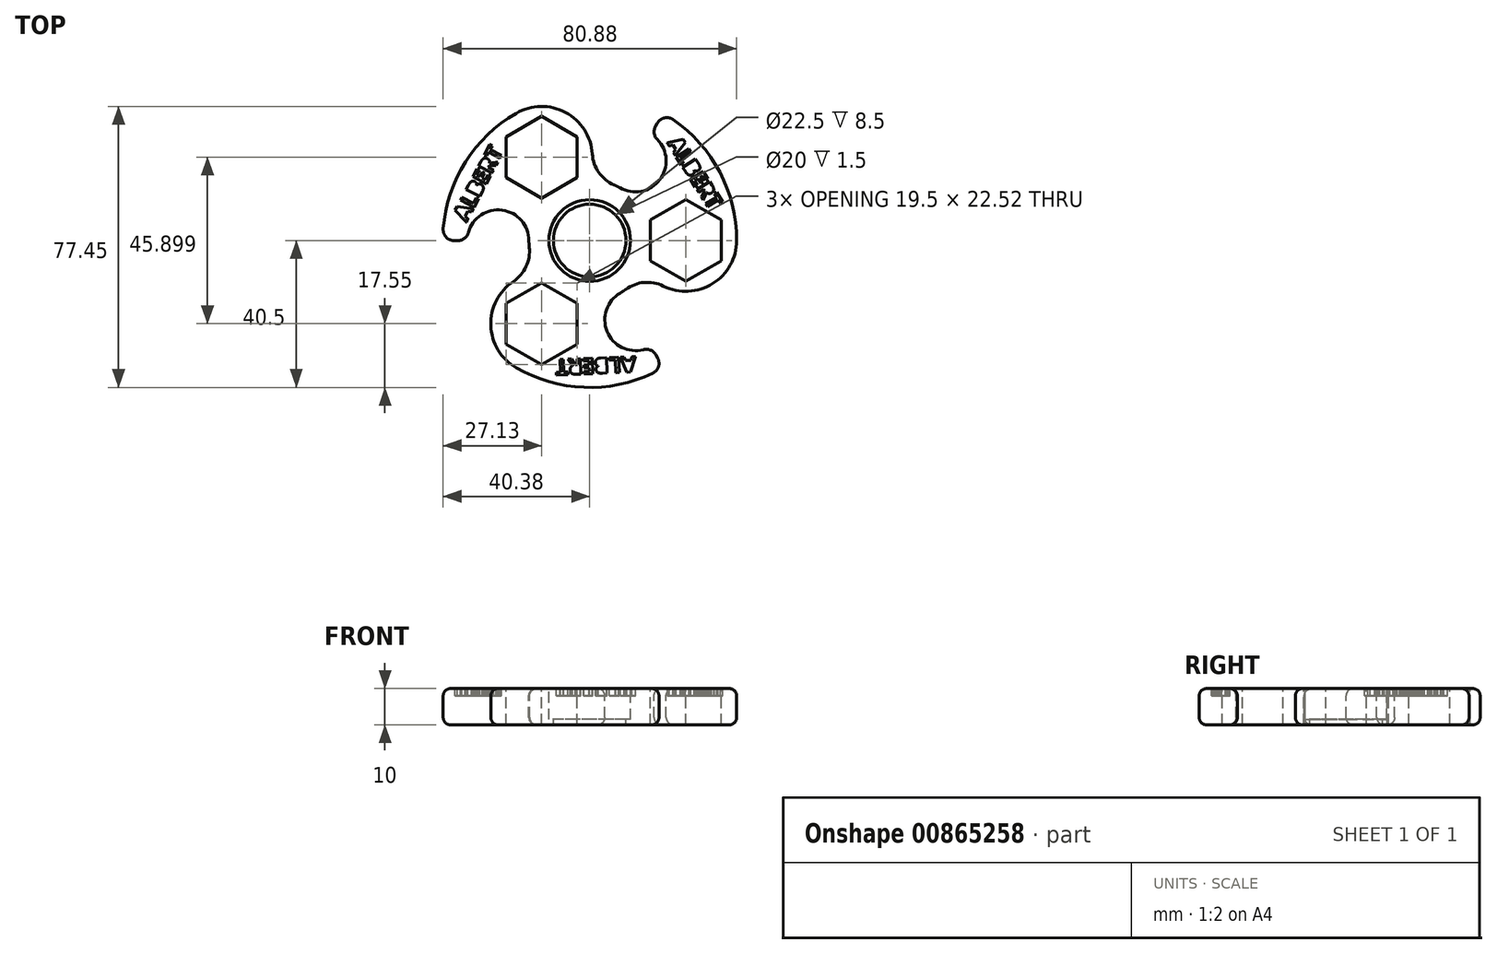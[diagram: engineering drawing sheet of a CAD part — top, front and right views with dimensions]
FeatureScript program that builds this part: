
annotation { "Feature Type Name" : "Feature", "Feature Type Description" : "" }
export const myFeature = defineFeature(function(context is Context, id is Id, definition is map)
    precondition{}
    {
        {
            var Q0;
            Q0=qCreatedBy(makeId("Top.planeOp"),FACE);
            var sketch = newSketch(context, id + "F0", { "sketchPlane" : qUnion([Q0])});
            skCircle(sketch, "E0", {"center": v(0, 0) * mm, "radius": 11.25 * mm});
            skCircle(sketch, "E1.cCircle", {"center": v(26.5, 0) * mm, "radius": 9.75 * mm, "construction": true});
            skLineSegment(sketch, "E1.0", {"start": v(36.25, 5.63) * mm, "end": v(36.25, -5.63) * mm});
            skLineSegment(sketch, "E1.1", {"start": v(36.25, -5.63) * mm, "end": v(26.5, -11.26) * mm});
            skLineSegment(sketch, "E1.2", {"start": v(26.5, -11.26) * mm, "end": v(16.75, -5.63) * mm});
            skLineSegment(sketch, "E1.3", {"start": v(16.75, -5.63) * mm, "end": v(16.75, 5.63) * mm});
            skLineSegment(sketch, "E1.4", {"start": v(16.75, 5.63) * mm, "end": v(26.5, 11.26) * mm});
            skLineSegment(sketch, "E1.5", {"start": v(26.5, 11.26) * mm, "end": v(36.25, 5.63) * mm});
            skPoint(sketch, "E1.0.midPoint", {"position": v(9.75, 0) * mm});
            skLineSegment(sketch, "E2", {"start": v(26.5, 11.26) * mm, "end": v(16.75, 5.63) * mm});
            skLineSegment(sketch, "E3", {"start": v(16.75, 5.63) * mm, "end": v(16.75, -5.63) * mm});
            skLineSegment(sketch, "E4", {"start": v(16.75, -5.63) * mm, "end": v(26.5, -11.26) * mm});
            skLineSegment(sketch, "E5", {"start": v(26.5, -11.26) * mm, "end": v(36.25, -5.63) * mm});
            skLineSegment(sketch, "E6", {"start": v(36.25, -5.63) * mm, "end": v(36.25, 5.63) * mm});
            skLineSegment(sketch, "E7", {"start": v(36.25, 5.63) * mm, "end": v(26.5, 11.26) * mm});
            skArc(sketch, "E8", {"start": v(8.38, 14.5) * mm, "mid": v(7.55, 14.95) * mm, "end": v(6.7, 15.35) * mm});
            skArc(sketch, "E9", {"start": v(20.3, -12.56) * mm, "mid": v(33.9, -11.89) * mm, "end": v(40.5, 0) * mm});
            skArc(sketch, "E10", {"start": v(40.5, 0) * mm, "mid": v(35.85, 18.84) * mm, "end": v(22.97, 33.35) * mm});
            skLineSegment(sketch, "E11", {"start": v(8.32, 14.54) * mm, "end": v(8.32, 14.54) * mm});
            skArc(sketch, "E12", {"start": v(8.32, 14.54) * mm, "mid": v(19.3, 16.7) * mm, "end": v(18.62, 27.87) * mm});
            skLineSegment(sketch, "E13.trimOffspring", {"start": v(18.16, 31.5) * mm, "end": v(18.68, 32.39) * mm});
            skPoint(sketch, "E14.visualSharp", {"position": v(14.85, -7.76) * mm});
            skArc(sketch, "E14.filletArc", {"start": v(20.3, -12.56) * mm, "mid": v(15, -11.56) * mm, "end": v(9.95, -13.48) * mm});
            skPoint(sketch, "E15.visualSharp", {"position": v(20.24, 35.08) * mm});
            skArc(sketch, "E15.filletArc", {"start": v(22.97, 33.35) * mm, "mid": v(20.62, 33.8) * mm, "end": v(18.68, 32.39) * mm});
            skPoint(sketch, "E16.visualSharp", {"position": v(16.85, 29.24) * mm});
            skArc(sketch, "E16.filletArc", {"start": v(18.16, 31.5) * mm, "mid": v(17.78, 29.6) * mm, "end": v(18.62, 27.87) * mm});
            skArc(sketch, "E17.1.0", {"start": v(-16.75, -0.07) * mm, "mid": v(-24.11, 8.38) * mm, "end": v(-33.45, 2.19) * mm});
            skArc(sketch, "E17.1.1", {"start": v(-36.35, -0.02) * mm, "mid": v(-34.53, 0.6) * mm, "end": v(-33.45, 2.19) * mm});
            skLineSegment(sketch, "E17.1.2", {"start": v(-36.35, -0.02) * mm, "end": v(-37.39, -0.02) * mm});
            skArc(sketch, "E17.1.3", {"start": v(-40.37, 3.22) * mm, "mid": v(-39.59, 0.95) * mm, "end": v(-37.39, -0.02) * mm});
            skArc(sketch, "E17.1.4", {"start": v(-20.25, 35.07) * mm, "mid": v(-34.24, 21.63) * mm, "end": v(-40.37, 3.22) * mm});
            skArc(sketch, "E17.1.5", {"start": v(0.72, 23.86) * mm, "mid": v(-6.65, 35.3) * mm, "end": v(-20.25, 35.07) * mm});
            skArc(sketch, "E17.1.6", {"start": v(0.72, 23.86) * mm, "mid": v(2.52, 18.77) * mm, "end": v(6.7, 15.35) * mm});
            skLineSegment(sketch, "E17.1.7", {"start": v(-3.5, 17.32) * mm, "end": v(-3.5, 28.58) * mm});
            skLineSegment(sketch, "E17.1.8", {"start": v(-3.5, 28.58) * mm, "end": v(-13.25, 34.2) * mm});
            skLineSegment(sketch, "E17.1.9", {"start": v(-13.25, 34.2) * mm, "end": v(-23, 28.58) * mm});
            skLineSegment(sketch, "E17.1.10", {"start": v(-23, 28.58) * mm, "end": v(-23, 17.32) * mm});
            skLineSegment(sketch, "E17.1.11", {"start": v(-23, 17.32) * mm, "end": v(-13.25, 11.7) * mm});
            skLineSegment(sketch, "E17.1.12", {"start": v(-13.25, 11.7) * mm, "end": v(-3.5, 17.32) * mm});
            skArc(sketch, "E17.2.0", {"start": v(8.43, -14.47) * mm, "mid": v(4.8, -25.07) * mm, "end": v(14.83, -30.06) * mm});
            skArc(sketch, "E17.2.1", {"start": v(18.2, -31.47) * mm, "mid": v(16.75, -30.2) * mm, "end": v(14.83, -30.06) * mm});
            skLineSegment(sketch, "E17.2.2", {"start": v(18.2, -31.47) * mm, "end": v(18.71, -32.37) * mm});
            skArc(sketch, "E17.2.3", {"start": v(17.4, -36.57) * mm, "mid": v(18.97, -34.76) * mm, "end": v(18.71, -32.37) * mm});
            skArc(sketch, "E17.2.4", {"start": v(-20.25, -35.07) * mm, "mid": v(-1.61, -40.47) * mm, "end": v(17.4, -36.57) * mm});
            skArc(sketch, "E17.2.5", {"start": v(-21.03, -11.3) * mm, "mid": v(-27.24, -23.4) * mm, "end": v(-20.25, -35.07) * mm});
            skArc(sketch, "E17.2.6", {"start": v(-21.03, -11.3) * mm, "mid": v(-17.51, -7.2) * mm, "end": v(-16.64, -1.87) * mm});
            skLineSegment(sketch, "E17.2.7", {"start": v(-13.25, -11.7) * mm, "end": v(-23, -17.32) * mm});
            skLineSegment(sketch, "E17.2.8", {"start": v(-23, -17.32) * mm, "end": v(-23, -28.58) * mm});
            skLineSegment(sketch, "E17.2.9", {"start": v(-23, -28.58) * mm, "end": v(-13.25, -34.2) * mm});
            skLineSegment(sketch, "E17.2.10", {"start": v(-13.25, -34.2) * mm, "end": v(-3.5, -28.58) * mm});
            skLineSegment(sketch, "E17.2.11", {"start": v(-3.5, -28.58) * mm, "end": v(-3.5, -17.32) * mm});
            skLineSegment(sketch, "E17.2.12", {"start": v(-3.5, -17.32) * mm, "end": v(-13.25, -11.7) * mm});
            skArc(sketch, "E18.trimOffspring", {"start": v(-16.75, 0) * mm, "mid": v(-16.72, -0.94) * mm, "end": v(-16.64, -1.87) * mm});
            skArc(sketch, "E19.trimOffspring", {"start": v(8.37, -14.5) * mm, "mid": v(9.17, -14.02) * mm, "end": v(9.95, -13.48) * mm});
            skSolve(sketch);
        }
        {
            var Q0;
            Q0=qCreatedBy(makeId("Top.planeOp"),FACE);
            cPlane(context, id + "F1", {"entities" : qUnion([Q0]), "cplaneType" : CPlaneType.OFFSET, "offset" : 5 * mm, "width" : 150 * mm, "height" : 150 * mm});
        }
        {
            var Q0;
            Q0=qCreatedBy(id+"F1.planeOp",FACE);
            var sketch = newSketch(context, id + "F2", { "sketchPlane" : qUnion([Q0])});
            skText(sketch, "E20", { "text": "ALBERT", "fontName": "OpenSans-Bold.ttf"});
            const initialGuessF2  = {"E20": [0.0214, 0.0269, 0.53415, -0.84539, 0.00426]};
            skSetInitialGuess(sketch, initialGuessF2);
            skSolve(sketch);
        }
        {
            var Q0;
            Q0=qCreatedBy(makeId("Top.planeOp"),FACE);
            var sketch = newSketch(context, id + "F3", { "sketchPlane" : qUnion([Q0])});
            skCircle(sketch, "E21", {"center": v(0, 0) * mm, "radius": 11.25 * mm});
            skCircle(sketch, "E22", {"center": v(0, 0) * mm, "radius": 10 * mm});
            skSolve(sketch);
        }
        {
            var Q0;
            Q0=makeQuery(id+"F0.imprint","IMPRINT",FACE,{"disambiguationData":[TD([[makeQuery(id+"F0.imprint","IMPRINT",EDGE,{"derivedFrom":sQuery(id+"F0.wireOp",EDGE,"E0")}),-1.0]])]});
            extrude(context, id + "F4", {"entities" : qUnion([Q0]), "depth" : -10 * mm, "offsetDistance" : 25 * mm});
        }
        {
            var Q0;
            Q0=makeQuery(id+"F3.imprint","IMPRINT",FACE,{"disambiguationData":[TD([[makeQuery(id+"F3.imprint","IMPRINT",EDGE,{"derivedFrom":sQuery(id+"F3.wireOp",EDGE,"E21")}),1.0]])]});
            extrude(context, id + "F5", {"entities" : qUnion([Q0]), "oppositeDirection" : true, "depth" : 1 * mm, "offsetDistance" : 25 * mm});
        }
        {
            var Q0;
            Q0=qSketchRegion(id+"F2",true);
            extrude(context, id + "F6", {"entities" : qUnion([Q0]), "depth" : -7 * mm, "offsetDistance" : 25 * mm});
        }
        {
            var Q0;
            Q0=makeQuery(id+"F4.opExtrude","CAP_EDGE",EDGE,{"disambiguationData":[OSD([sQuery(id+"F0.wireOp",EDGE,"E17.1.4")])],"isStart":true});
            var Q1;
            Q1=makeQuery(id+"F4.opExtrude","CAP_EDGE",EDGE,{"disambiguationData":[OSD([sQuery(id+"F0.wireOp",EDGE,"E17.1.5")])],"isStart":true});
            var Q2;
            Q2=makeQuery(id+"F4.opExtrude","CAP_EDGE",EDGE,{"disambiguationData":[OSD([sQuery(id+"F0.wireOp",EDGE,"E12")])],"isStart":true});
            var Q3;
            Q3=makeQuery(id+"F4.opExtrude","CAP_EDGE",EDGE,{"disambiguationData":[OSD([sQuery(id+"F0.wireOp",EDGE,"E17.2.2")])],"isStart":true});
            fillet(context, id + "F7", {"entities" : qUnion([Q0, Q1, Q2, Q3]), "radius" : 2 * mm, "tangentPropagation" : true, "allowEdgeOverflow" : false});
        }
        {
            var Q0;
            Q0=makeQuery(id+"F4.opExtrude","CAP_EDGE",EDGE,{"disambiguationData":[OSD([sQuery(id+"F0.wireOp",EDGE,"E17.2.4")])],"isStart":false});
            var Q1;
            Q1=makeQuery(id+"F4.opExtrude","CAP_EDGE",EDGE,{"disambiguationData":[OSD([sQuery(id+"F0.wireOp",EDGE,"E17.2.3")])],"isStart":false});
            var Q2;
            Q2=makeQuery(id+"F4.opExtrude","CAP_EDGE",EDGE,{"disambiguationData":[OSD([sQuery(id+"F0.wireOp",EDGE,"E9")])],"isStart":false});
            var Q3;
            Q3=makeQuery(id+"F4.opExtrude","CAP_EDGE",EDGE,{"disambiguationData":[OSD([sQuery(id+"F0.wireOp",EDGE,"E17.1.5")])],"isStart":false});
            fillet(context, id + "F8", {"entities" : qUnion([Q0, Q1, Q2, Q3]), "radius" : 2 * mm, "tangentPropagation" : true, "allowEdgeOverflow" : false});
        }
        {
            var Q0;
            Q0=makeQuery(id+"F6.opExtrude","SWEPT_BODY",BODY,{"disambiguationData":[OSD([sQuery(id+"F2.wireOp",EDGE,"E20.sketch_text.stroke-74"),sQuery(id+"F2.wireOp",EDGE,"E20.sketch_text.stroke-75"),sQuery(id+"F2.wireOp",EDGE,"E20.sketch_text.stroke-76"),sQuery(id+"F2.wireOp",EDGE,"E20.sketch_text.stroke-77"),sQuery(id+"F2.wireOp",EDGE,"E20.sketch_text.stroke-78"),sQuery(id+"F2.wireOp",EDGE,"E20.sketch_text.stroke-79"),sQuery(id+"F2.wireOp",EDGE,"E20.sketch_text.stroke-80"),sQuery(id+"F2.wireOp",EDGE,"E20.sketch_text.stroke-81")])]});
            var Q1;
            Q1=makeQuery(id+"F6.opExtrude","SWEPT_BODY",BODY,{"disambiguationData":[OSD([sQuery(id+"F2.wireOp",EDGE,"E20.sketch_text.stroke-55"),sQuery(id+"F2.wireOp",EDGE,"E20.sketch_text.stroke-56"),sQuery(id+"F2.wireOp",EDGE,"E20.sketch_text.stroke-57"),sQuery(id+"F2.wireOp",EDGE,"E20.sketch_text.stroke-58"),sQuery(id+"F2.wireOp",EDGE,"E20.sketch_text.stroke-59"),sQuery(id+"F2.wireOp",EDGE,"E20.sketch_text.stroke-60"),sQuery(id+"F2.wireOp",EDGE,"E20.sketch_text.stroke-61"),sQuery(id+"F2.wireOp",EDGE,"E20.sketch_text.stroke-62"),sQuery(id+"F2.wireOp",EDGE,"E20.sketch_text.stroke-63"),sQuery(id+"F2.wireOp",EDGE,"E20.sketch_text.stroke-64"),sQuery(id+"F2.wireOp",EDGE,"E20.sketch_text.stroke-65"),sQuery(id+"F2.wireOp",EDGE,"E20.sketch_text.stroke-66"),sQuery(id+"F2.wireOp",EDGE,"E20.sketch_text.stroke-67"),sQuery(id+"F2.wireOp",EDGE,"E20.sketch_text.stroke-68"),sQuery(id+"F2.wireOp",EDGE,"E20.sketch_text.stroke-69"),sQuery(id+"F2.wireOp",EDGE,"E20.sketch_text.stroke-70"),sQuery(id+"F2.wireOp",EDGE,"E20.sketch_text.stroke-71"),sQuery(id+"F2.wireOp",EDGE,"E20.sketch_text.stroke-72"),sQuery(id+"F2.wireOp",EDGE,"E20.sketch_text.stroke-73")])]});
            var Q2;
            Q2=makeQuery(id+"F6.opExtrude","SWEPT_BODY",BODY,{"disambiguationData":[OSD([sQuery(id+"F2.wireOp",EDGE,"E20.sketch_text.stroke-43"),sQuery(id+"F2.wireOp",EDGE,"E20.sketch_text.stroke-44"),sQuery(id+"F2.wireOp",EDGE,"E20.sketch_text.stroke-45"),sQuery(id+"F2.wireOp",EDGE,"E20.sketch_text.stroke-46"),sQuery(id+"F2.wireOp",EDGE,"E20.sketch_text.stroke-47"),sQuery(id+"F2.wireOp",EDGE,"E20.sketch_text.stroke-48"),sQuery(id+"F2.wireOp",EDGE,"E20.sketch_text.stroke-49"),sQuery(id+"F2.wireOp",EDGE,"E20.sketch_text.stroke-50"),sQuery(id+"F2.wireOp",EDGE,"E20.sketch_text.stroke-51"),sQuery(id+"F2.wireOp",EDGE,"E20.sketch_text.stroke-52"),sQuery(id+"F2.wireOp",EDGE,"E20.sketch_text.stroke-53"),sQuery(id+"F2.wireOp",EDGE,"E20.sketch_text.stroke-54")])]});
            var Q3;
            Q3=makeQuery(id+"F6.opExtrude","SWEPT_BODY",BODY,{"disambiguationData":[OSD([sQuery(id+"F2.wireOp",EDGE,"E20.sketch_text.stroke-18"),sQuery(id+"F2.wireOp",EDGE,"E20.sketch_text.stroke-19"),sQuery(id+"F2.wireOp",EDGE,"E20.sketch_text.stroke-20"),sQuery(id+"F2.wireOp",EDGE,"E20.sketch_text.stroke-21"),sQuery(id+"F2.wireOp",EDGE,"E20.sketch_text.stroke-22"),sQuery(id+"F2.wireOp",EDGE,"E20.sketch_text.stroke-23"),sQuery(id+"F2.wireOp",EDGE,"E20.sketch_text.stroke-24"),sQuery(id+"F2.wireOp",EDGE,"E20.sketch_text.stroke-25"),sQuery(id+"F2.wireOp",EDGE,"E20.sketch_text.stroke-26"),sQuery(id+"F2.wireOp",EDGE,"E20.sketch_text.stroke-27"),sQuery(id+"F2.wireOp",EDGE,"E20.sketch_text.stroke-28"),sQuery(id+"F2.wireOp",EDGE,"E20.sketch_text.stroke-29"),sQuery(id+"F2.wireOp",EDGE,"E20.sketch_text.stroke-30"),sQuery(id+"F2.wireOp",EDGE,"E20.sketch_text.stroke-31"),sQuery(id+"F2.wireOp",EDGE,"E20.sketch_text.stroke-32"),sQuery(id+"F2.wireOp",EDGE,"E20.sketch_text.stroke-33"),sQuery(id+"F2.wireOp",EDGE,"E20.sketch_text.stroke-34"),sQuery(id+"F2.wireOp",EDGE,"E20.sketch_text.stroke-35"),sQuery(id+"F2.wireOp",EDGE,"E20.sketch_text.stroke-36"),sQuery(id+"F2.wireOp",EDGE,"E20.sketch_text.stroke-37"),sQuery(id+"F2.wireOp",EDGE,"E20.sketch_text.stroke-38"),sQuery(id+"F2.wireOp",EDGE,"E20.sketch_text.stroke-39"),sQuery(id+"F2.wireOp",EDGE,"E20.sketch_text.stroke-40"),sQuery(id+"F2.wireOp",EDGE,"E20.sketch_text.stroke-41"),sQuery(id+"F2.wireOp",EDGE,"E20.sketch_text.stroke-42")])]});
            var Q4;
            Q4=makeQuery(id+"F6.opExtrude","SWEPT_BODY",BODY,{"disambiguationData":[OSD([sQuery(id+"F2.wireOp",EDGE,"E20.sketch_text.stroke-0"),sQuery(id+"F2.wireOp",EDGE,"E20.sketch_text.stroke-1"),sQuery(id+"F2.wireOp",EDGE,"E20.sketch_text.stroke-2"),sQuery(id+"F2.wireOp",EDGE,"E20.sketch_text.stroke-3"),sQuery(id+"F2.wireOp",EDGE,"E20.sketch_text.stroke-4"),sQuery(id+"F2.wireOp",EDGE,"E20.sketch_text.stroke-5"),sQuery(id+"F2.wireOp",EDGE,"E20.sketch_text.stroke-6"),sQuery(id+"F2.wireOp",EDGE,"E20.sketch_text.stroke-7"),sQuery(id+"F2.wireOp",EDGE,"E20.sketch_text.stroke-8"),sQuery(id+"F2.wireOp",EDGE,"E20.sketch_text.stroke-9"),sQuery(id+"F2.wireOp",EDGE,"E20.sketch_text.stroke-10"),sQuery(id+"F2.wireOp",EDGE,"E20.sketch_text.stroke-11")])]});
            var Q5;
            Q5=makeQuery(id+"F6.opExtrude","SWEPT_BODY",BODY,{"disambiguationData":[OSD([sQuery(id+"F2.wireOp",EDGE,"E20.sketch_text.stroke-12"),sQuery(id+"F2.wireOp",EDGE,"E20.sketch_text.stroke-13"),sQuery(id+"F2.wireOp",EDGE,"E20.sketch_text.stroke-14"),sQuery(id+"F2.wireOp",EDGE,"E20.sketch_text.stroke-15"),sQuery(id+"F2.wireOp",EDGE,"E20.sketch_text.stroke-16"),sQuery(id+"F2.wireOp",EDGE,"E20.sketch_text.stroke-17")])]});
            var Q6;
            Q6=makeQuery(id+"F5.opExtrude","CAP_EDGE",EDGE,{"disambiguationData":[OSD([sQuery(id+"F3.wireOp",EDGE,"E22")])],"isStart":false});
            circularPattern(context, id + "F9", {"operationType" : NewBodyOperationType.REMOVE, "entities" : qUnion([Q0, Q1, Q2, Q3, Q4, Q5]), "axis" : qUnion([Q6]), "angle" : 360 * degree, "instanceCount" : 3, "equalSpace" : true, "computeTransformsWithoutBuiltin" : true});
        }
        {
            var Q0;
            Q0=makeQuery(id+"F5.opExtrude","SWEPT_BODY",BODY,{"disambiguationData":[OSD([sQuery(id+"F3.wireOp",EDGE,"E21"),sQuery(id+"F3.wireOp",EDGE,"E22")])]});
            transform(context, id + "F10", {"entities" : qUnion([Q0]), "transformType" : TransformType.TRANSLATION_3D, "dx" : 0 * mm, "dy" : 0 * mm, "dz" : -9 * mm, "makeCopy" : false});
        }
        {
            var Q0;
            Q0=makeQuery(id+"F9.boolean.opBoolean","SPLIT",FACE,{"disambiguationData":[TD([makeQuery(id+"F9.opPattern","COPY",FACE,{"derivedFrom":makeQuery(id+"F6.opExtrude","SWEPT_FACE",FACE,{"disambiguationData":[OSD([sQuery(id+"F2.wireOp",EDGE,"E20.sketch_text.stroke-8")])]}),"instanceName":"1"})])],"derivedFrom":makeQuery(id+"F4.opExtrude","CAP_FACE",FACE,{"disambiguationData":[OSD([sQuery(id+"F0.wireOp",EDGE,"E0"),sQuery(id+"F0.wireOp",EDGE,"E2"),sQuery(id+"F0.wireOp",EDGE,"E3"),sQuery(id+"F0.wireOp",EDGE,"E4"),sQuery(id+"F0.wireOp",EDGE,"E5"),sQuery(id+"F0.wireOp",EDGE,"E6"),sQuery(id+"F0.wireOp",EDGE,"E7"),sQuery(id+"F0.wireOp",EDGE,"E8"),sQuery(id+"F0.wireOp",EDGE,"E9"),sQuery(id+"F0.wireOp",EDGE,"E10"),sQuery(id+"F0.wireOp",EDGE,"E12"),sQuery(id+"F0.wireOp",EDGE,"E13.trimOffspring"),sQuery(id+"F0.wireOp",EDGE,"E14.filletArc"),sQuery(id+"F0.wireOp",EDGE,"E15.filletArc"),sQuery(id+"F0.wireOp",EDGE,"E16.filletArc"),sQuery(id+"F0.wireOp",EDGE,"E17.1.0"),sQuery(id+"F0.wireOp",EDGE,"E17.1.1"),sQuery(id+"F0.wireOp",EDGE,"E17.1.2"),sQuery(id+"F0.wireOp",EDGE,"E17.1.3"),sQuery(id+"F0.wireOp",EDGE,"E17.1.4"),sQuery(id+"F0.wireOp",EDGE,"E17.1.5"),sQuery(id+"F0.wireOp",EDGE,"E17.1.6"),sQuery(id+"F0.wireOp",EDGE,"E17.1.7"),sQuery(id+"F0.wireOp",EDGE,"E17.1.8"),sQuery(id+"F0.wireOp",EDGE,"E17.1.9"),sQuery(id+"F0.wireOp",EDGE,"E17.1.10"),sQuery(id+"F0.wireOp",EDGE,"E17.1.11"),sQuery(id+"F0.wireOp",EDGE,"E17.1.12"),sQuery(id+"F0.wireOp",EDGE,"E17.2.0"),sQuery(id+"F0.wireOp",EDGE,"E17.2.1"),sQuery(id+"F0.wireOp",EDGE,"E17.2.2"),sQuery(id+"F0.wireOp",EDGE,"E17.2.3"),sQuery(id+"F0.wireOp",EDGE,"E17.2.4"),sQuery(id+"F0.wireOp",EDGE,"E17.2.5"),sQuery(id+"F0.wireOp",EDGE,"E17.2.6"),sQuery(id+"F0.wireOp",EDGE,"E17.2.7"),sQuery(id+"F0.wireOp",EDGE,"E17.2.8"),sQuery(id+"F0.wireOp",EDGE,"E17.2.9"),sQuery(id+"F0.wireOp",EDGE,"E17.2.10"),sQuery(id+"F0.wireOp",EDGE,"E17.2.11"),sQuery(id+"F0.wireOp",EDGE,"E17.2.12"),sQuery(id+"F0.wireOp",EDGE,"E18.trimOffspring"),sQuery(id+"F0.wireOp",EDGE,"E19.trimOffspring")])],"isStart":true})});
            var Q1;
            Q1=makeQuery(id+"F9.boolean.opBoolean","SPLIT",FACE,{"disambiguationData":[TD([makeQuery(id+"F9.opPattern","COPY",FACE,{"derivedFrom":makeQuery(id+"F6.opExtrude","SWEPT_FACE",FACE,{"disambiguationData":[OSD([sQuery(id+"F2.wireOp",EDGE,"E20.sketch_text.stroke-30")])]}),"instanceName":"1"})])],"derivedFrom":makeQuery(id+"F4.opExtrude","CAP_FACE",FACE,{"disambiguationData":[OSD([sQuery(id+"F0.wireOp",EDGE,"E0"),sQuery(id+"F0.wireOp",EDGE,"E2"),sQuery(id+"F0.wireOp",EDGE,"E3"),sQuery(id+"F0.wireOp",EDGE,"E4"),sQuery(id+"F0.wireOp",EDGE,"E5"),sQuery(id+"F0.wireOp",EDGE,"E6"),sQuery(id+"F0.wireOp",EDGE,"E7"),sQuery(id+"F0.wireOp",EDGE,"E8"),sQuery(id+"F0.wireOp",EDGE,"E9"),sQuery(id+"F0.wireOp",EDGE,"E10"),sQuery(id+"F0.wireOp",EDGE,"E12"),sQuery(id+"F0.wireOp",EDGE,"E13.trimOffspring"),sQuery(id+"F0.wireOp",EDGE,"E14.filletArc"),sQuery(id+"F0.wireOp",EDGE,"E15.filletArc"),sQuery(id+"F0.wireOp",EDGE,"E16.filletArc"),sQuery(id+"F0.wireOp",EDGE,"E17.1.0"),sQuery(id+"F0.wireOp",EDGE,"E17.1.1"),sQuery(id+"F0.wireOp",EDGE,"E17.1.2"),sQuery(id+"F0.wireOp",EDGE,"E17.1.3"),sQuery(id+"F0.wireOp",EDGE,"E17.1.4"),sQuery(id+"F0.wireOp",EDGE,"E17.1.5"),sQuery(id+"F0.wireOp",EDGE,"E17.1.6"),sQuery(id+"F0.wireOp",EDGE,"E17.1.7"),sQuery(id+"F0.wireOp",EDGE,"E17.1.8"),sQuery(id+"F0.wireOp",EDGE,"E17.1.9"),sQuery(id+"F0.wireOp",EDGE,"E17.1.10"),sQuery(id+"F0.wireOp",EDGE,"E17.1.11"),sQuery(id+"F0.wireOp",EDGE,"E17.1.12"),sQuery(id+"F0.wireOp",EDGE,"E17.2.0"),sQuery(id+"F0.wireOp",EDGE,"E17.2.1"),sQuery(id+"F0.wireOp",EDGE,"E17.2.2"),sQuery(id+"F0.wireOp",EDGE,"E17.2.3"),sQuery(id+"F0.wireOp",EDGE,"E17.2.4"),sQuery(id+"F0.wireOp",EDGE,"E17.2.5"),sQuery(id+"F0.wireOp",EDGE,"E17.2.6"),sQuery(id+"F0.wireOp",EDGE,"E17.2.7"),sQuery(id+"F0.wireOp",EDGE,"E17.2.8"),sQuery(id+"F0.wireOp",EDGE,"E17.2.9"),sQuery(id+"F0.wireOp",EDGE,"E17.2.10"),sQuery(id+"F0.wireOp",EDGE,"E17.2.11"),sQuery(id+"F0.wireOp",EDGE,"E17.2.12"),sQuery(id+"F0.wireOp",EDGE,"E18.trimOffspring"),sQuery(id+"F0.wireOp",EDGE,"E19.trimOffspring")])],"isStart":true})});
            var Q2;
            Q2=makeQuery(id+"F9.boolean.opBoolean","SPLIT",FACE,{"disambiguationData":[TD([makeQuery(id+"F9.opPattern","COPY",FACE,{"derivedFrom":makeQuery(id+"F6.opExtrude","SWEPT_FACE",FACE,{"disambiguationData":[OSD([sQuery(id+"F2.wireOp",EDGE,"E20.sketch_text.stroke-37")])]}),"instanceName":"1"})])],"derivedFrom":makeQuery(id+"F4.opExtrude","CAP_FACE",FACE,{"disambiguationData":[OSD([sQuery(id+"F0.wireOp",EDGE,"E0"),sQuery(id+"F0.wireOp",EDGE,"E2"),sQuery(id+"F0.wireOp",EDGE,"E3"),sQuery(id+"F0.wireOp",EDGE,"E4"),sQuery(id+"F0.wireOp",EDGE,"E5"),sQuery(id+"F0.wireOp",EDGE,"E6"),sQuery(id+"F0.wireOp",EDGE,"E7"),sQuery(id+"F0.wireOp",EDGE,"E8"),sQuery(id+"F0.wireOp",EDGE,"E9"),sQuery(id+"F0.wireOp",EDGE,"E10"),sQuery(id+"F0.wireOp",EDGE,"E12"),sQuery(id+"F0.wireOp",EDGE,"E13.trimOffspring"),sQuery(id+"F0.wireOp",EDGE,"E14.filletArc"),sQuery(id+"F0.wireOp",EDGE,"E15.filletArc"),sQuery(id+"F0.wireOp",EDGE,"E16.filletArc"),sQuery(id+"F0.wireOp",EDGE,"E17.1.0"),sQuery(id+"F0.wireOp",EDGE,"E17.1.1"),sQuery(id+"F0.wireOp",EDGE,"E17.1.2"),sQuery(id+"F0.wireOp",EDGE,"E17.1.3"),sQuery(id+"F0.wireOp",EDGE,"E17.1.4"),sQuery(id+"F0.wireOp",EDGE,"E17.1.5"),sQuery(id+"F0.wireOp",EDGE,"E17.1.6"),sQuery(id+"F0.wireOp",EDGE,"E17.1.7"),sQuery(id+"F0.wireOp",EDGE,"E17.1.8"),sQuery(id+"F0.wireOp",EDGE,"E17.1.9"),sQuery(id+"F0.wireOp",EDGE,"E17.1.10"),sQuery(id+"F0.wireOp",EDGE,"E17.1.11"),sQuery(id+"F0.wireOp",EDGE,"E17.1.12"),sQuery(id+"F0.wireOp",EDGE,"E17.2.0"),sQuery(id+"F0.wireOp",EDGE,"E17.2.1"),sQuery(id+"F0.wireOp",EDGE,"E17.2.2"),sQuery(id+"F0.wireOp",EDGE,"E17.2.3"),sQuery(id+"F0.wireOp",EDGE,"E17.2.4"),sQuery(id+"F0.wireOp",EDGE,"E17.2.5"),sQuery(id+"F0.wireOp",EDGE,"E17.2.6"),sQuery(id+"F0.wireOp",EDGE,"E17.2.7"),sQuery(id+"F0.wireOp",EDGE,"E17.2.8"),sQuery(id+"F0.wireOp",EDGE,"E17.2.9"),sQuery(id+"F0.wireOp",EDGE,"E17.2.10"),sQuery(id+"F0.wireOp",EDGE,"E17.2.11"),sQuery(id+"F0.wireOp",EDGE,"E17.2.12"),sQuery(id+"F0.wireOp",EDGE,"E18.trimOffspring"),sQuery(id+"F0.wireOp",EDGE,"E19.trimOffspring")])],"isStart":true})});
            var Q3;
            Q3=makeQuery(id+"F9.boolean.opBoolean","SPLIT",FACE,{"disambiguationData":[TD([makeQuery(id+"F9.opPattern","COPY",FACE,{"derivedFrom":makeQuery(id+"F6.opExtrude","SWEPT_FACE",FACE,{"disambiguationData":[OSD([sQuery(id+"F2.wireOp",EDGE,"E20.sketch_text.stroke-55")])]}),"instanceName":"1"})])],"derivedFrom":makeQuery(id+"F4.opExtrude","CAP_FACE",FACE,{"disambiguationData":[OSD([sQuery(id+"F0.wireOp",EDGE,"E0"),sQuery(id+"F0.wireOp",EDGE,"E2"),sQuery(id+"F0.wireOp",EDGE,"E3"),sQuery(id+"F0.wireOp",EDGE,"E4"),sQuery(id+"F0.wireOp",EDGE,"E5"),sQuery(id+"F0.wireOp",EDGE,"E6"),sQuery(id+"F0.wireOp",EDGE,"E7"),sQuery(id+"F0.wireOp",EDGE,"E8"),sQuery(id+"F0.wireOp",EDGE,"E9"),sQuery(id+"F0.wireOp",EDGE,"E10"),sQuery(id+"F0.wireOp",EDGE,"E12"),sQuery(id+"F0.wireOp",EDGE,"E13.trimOffspring"),sQuery(id+"F0.wireOp",EDGE,"E14.filletArc"),sQuery(id+"F0.wireOp",EDGE,"E15.filletArc"),sQuery(id+"F0.wireOp",EDGE,"E16.filletArc"),sQuery(id+"F0.wireOp",EDGE,"E17.1.0"),sQuery(id+"F0.wireOp",EDGE,"E17.1.1"),sQuery(id+"F0.wireOp",EDGE,"E17.1.2"),sQuery(id+"F0.wireOp",EDGE,"E17.1.3"),sQuery(id+"F0.wireOp",EDGE,"E17.1.4"),sQuery(id+"F0.wireOp",EDGE,"E17.1.5"),sQuery(id+"F0.wireOp",EDGE,"E17.1.6"),sQuery(id+"F0.wireOp",EDGE,"E17.1.7"),sQuery(id+"F0.wireOp",EDGE,"E17.1.8"),sQuery(id+"F0.wireOp",EDGE,"E17.1.9"),sQuery(id+"F0.wireOp",EDGE,"E17.1.10"),sQuery(id+"F0.wireOp",EDGE,"E17.1.11"),sQuery(id+"F0.wireOp",EDGE,"E17.1.12"),sQuery(id+"F0.wireOp",EDGE,"E17.2.0"),sQuery(id+"F0.wireOp",EDGE,"E17.2.1"),sQuery(id+"F0.wireOp",EDGE,"E17.2.2"),sQuery(id+"F0.wireOp",EDGE,"E17.2.3"),sQuery(id+"F0.wireOp",EDGE,"E17.2.4"),sQuery(id+"F0.wireOp",EDGE,"E17.2.5"),sQuery(id+"F0.wireOp",EDGE,"E17.2.6"),sQuery(id+"F0.wireOp",EDGE,"E17.2.7"),sQuery(id+"F0.wireOp",EDGE,"E17.2.8"),sQuery(id+"F0.wireOp",EDGE,"E17.2.9"),sQuery(id+"F0.wireOp",EDGE,"E17.2.10"),sQuery(id+"F0.wireOp",EDGE,"E17.2.11"),sQuery(id+"F0.wireOp",EDGE,"E17.2.12"),sQuery(id+"F0.wireOp",EDGE,"E18.trimOffspring"),sQuery(id+"F0.wireOp",EDGE,"E19.trimOffspring")])],"isStart":true})});
            var Q4;
            Q4=makeQuery(id+"F9.boolean.opBoolean","SPLIT",FACE,{"disambiguationData":[TD([makeQuery(id+"F6.opExtrude","SWEPT_FACE",FACE,{"disambiguationData":[OSD([sQuery(id+"F2.wireOp",EDGE,"E20.sketch_text.stroke-8")])]})])],"derivedFrom":makeQuery(id+"F4.opExtrude","CAP_FACE",FACE,{"disambiguationData":[OSD([sQuery(id+"F0.wireOp",EDGE,"E0"),sQuery(id+"F0.wireOp",EDGE,"E2"),sQuery(id+"F0.wireOp",EDGE,"E3"),sQuery(id+"F0.wireOp",EDGE,"E4"),sQuery(id+"F0.wireOp",EDGE,"E5"),sQuery(id+"F0.wireOp",EDGE,"E6"),sQuery(id+"F0.wireOp",EDGE,"E7"),sQuery(id+"F0.wireOp",EDGE,"E8"),sQuery(id+"F0.wireOp",EDGE,"E9"),sQuery(id+"F0.wireOp",EDGE,"E10"),sQuery(id+"F0.wireOp",EDGE,"E12"),sQuery(id+"F0.wireOp",EDGE,"E13.trimOffspring"),sQuery(id+"F0.wireOp",EDGE,"E14.filletArc"),sQuery(id+"F0.wireOp",EDGE,"E15.filletArc"),sQuery(id+"F0.wireOp",EDGE,"E16.filletArc"),sQuery(id+"F0.wireOp",EDGE,"E17.1.0"),sQuery(id+"F0.wireOp",EDGE,"E17.1.1"),sQuery(id+"F0.wireOp",EDGE,"E17.1.2"),sQuery(id+"F0.wireOp",EDGE,"E17.1.3"),sQuery(id+"F0.wireOp",EDGE,"E17.1.4"),sQuery(id+"F0.wireOp",EDGE,"E17.1.5"),sQuery(id+"F0.wireOp",EDGE,"E17.1.6"),sQuery(id+"F0.wireOp",EDGE,"E17.1.7"),sQuery(id+"F0.wireOp",EDGE,"E17.1.8"),sQuery(id+"F0.wireOp",EDGE,"E17.1.9"),sQuery(id+"F0.wireOp",EDGE,"E17.1.10"),sQuery(id+"F0.wireOp",EDGE,"E17.1.11"),sQuery(id+"F0.wireOp",EDGE,"E17.1.12"),sQuery(id+"F0.wireOp",EDGE,"E17.2.0"),sQuery(id+"F0.wireOp",EDGE,"E17.2.1"),sQuery(id+"F0.wireOp",EDGE,"E17.2.2"),sQuery(id+"F0.wireOp",EDGE,"E17.2.3"),sQuery(id+"F0.wireOp",EDGE,"E17.2.4"),sQuery(id+"F0.wireOp",EDGE,"E17.2.5"),sQuery(id+"F0.wireOp",EDGE,"E17.2.6"),sQuery(id+"F0.wireOp",EDGE,"E17.2.7"),sQuery(id+"F0.wireOp",EDGE,"E17.2.8"),sQuery(id+"F0.wireOp",EDGE,"E17.2.9"),sQuery(id+"F0.wireOp",EDGE,"E17.2.10"),sQuery(id+"F0.wireOp",EDGE,"E17.2.11"),sQuery(id+"F0.wireOp",EDGE,"E17.2.12"),sQuery(id+"F0.wireOp",EDGE,"E18.trimOffspring"),sQuery(id+"F0.wireOp",EDGE,"E19.trimOffspring")])],"isStart":true})});
            var Q5;
            Q5=makeQuery(id+"F9.boolean.opBoolean","SPLIT",FACE,{"disambiguationData":[TD([makeQuery(id+"F6.opExtrude","SWEPT_FACE",FACE,{"disambiguationData":[OSD([sQuery(id+"F2.wireOp",EDGE,"E20.sketch_text.stroke-30")])]})])],"derivedFrom":makeQuery(id+"F4.opExtrude","CAP_FACE",FACE,{"disambiguationData":[OSD([sQuery(id+"F0.wireOp",EDGE,"E0"),sQuery(id+"F0.wireOp",EDGE,"E2"),sQuery(id+"F0.wireOp",EDGE,"E3"),sQuery(id+"F0.wireOp",EDGE,"E4"),sQuery(id+"F0.wireOp",EDGE,"E5"),sQuery(id+"F0.wireOp",EDGE,"E6"),sQuery(id+"F0.wireOp",EDGE,"E7"),sQuery(id+"F0.wireOp",EDGE,"E8"),sQuery(id+"F0.wireOp",EDGE,"E9"),sQuery(id+"F0.wireOp",EDGE,"E10"),sQuery(id+"F0.wireOp",EDGE,"E12"),sQuery(id+"F0.wireOp",EDGE,"E13.trimOffspring"),sQuery(id+"F0.wireOp",EDGE,"E14.filletArc"),sQuery(id+"F0.wireOp",EDGE,"E15.filletArc"),sQuery(id+"F0.wireOp",EDGE,"E16.filletArc"),sQuery(id+"F0.wireOp",EDGE,"E17.1.0"),sQuery(id+"F0.wireOp",EDGE,"E17.1.1"),sQuery(id+"F0.wireOp",EDGE,"E17.1.2"),sQuery(id+"F0.wireOp",EDGE,"E17.1.3"),sQuery(id+"F0.wireOp",EDGE,"E17.1.4"),sQuery(id+"F0.wireOp",EDGE,"E17.1.5"),sQuery(id+"F0.wireOp",EDGE,"E17.1.6"),sQuery(id+"F0.wireOp",EDGE,"E17.1.7"),sQuery(id+"F0.wireOp",EDGE,"E17.1.8"),sQuery(id+"F0.wireOp",EDGE,"E17.1.9"),sQuery(id+"F0.wireOp",EDGE,"E17.1.10"),sQuery(id+"F0.wireOp",EDGE,"E17.1.11"),sQuery(id+"F0.wireOp",EDGE,"E17.1.12"),sQuery(id+"F0.wireOp",EDGE,"E17.2.0"),sQuery(id+"F0.wireOp",EDGE,"E17.2.1"),sQuery(id+"F0.wireOp",EDGE,"E17.2.2"),sQuery(id+"F0.wireOp",EDGE,"E17.2.3"),sQuery(id+"F0.wireOp",EDGE,"E17.2.4"),sQuery(id+"F0.wireOp",EDGE,"E17.2.5"),sQuery(id+"F0.wireOp",EDGE,"E17.2.6"),sQuery(id+"F0.wireOp",EDGE,"E17.2.7"),sQuery(id+"F0.wireOp",EDGE,"E17.2.8"),sQuery(id+"F0.wireOp",EDGE,"E17.2.9"),sQuery(id+"F0.wireOp",EDGE,"E17.2.10"),sQuery(id+"F0.wireOp",EDGE,"E17.2.11"),sQuery(id+"F0.wireOp",EDGE,"E17.2.12"),sQuery(id+"F0.wireOp",EDGE,"E18.trimOffspring"),sQuery(id+"F0.wireOp",EDGE,"E19.trimOffspring")])],"isStart":true})});
            var Q6;
            Q6=makeQuery(id+"F9.boolean.opBoolean","SPLIT",FACE,{"disambiguationData":[TD([makeQuery(id+"F6.opExtrude","SWEPT_FACE",FACE,{"disambiguationData":[OSD([sQuery(id+"F2.wireOp",EDGE,"E20.sketch_text.stroke-37")])]})])],"derivedFrom":makeQuery(id+"F4.opExtrude","CAP_FACE",FACE,{"disambiguationData":[OSD([sQuery(id+"F0.wireOp",EDGE,"E0"),sQuery(id+"F0.wireOp",EDGE,"E2"),sQuery(id+"F0.wireOp",EDGE,"E3"),sQuery(id+"F0.wireOp",EDGE,"E4"),sQuery(id+"F0.wireOp",EDGE,"E5"),sQuery(id+"F0.wireOp",EDGE,"E6"),sQuery(id+"F0.wireOp",EDGE,"E7"),sQuery(id+"F0.wireOp",EDGE,"E8"),sQuery(id+"F0.wireOp",EDGE,"E9"),sQuery(id+"F0.wireOp",EDGE,"E10"),sQuery(id+"F0.wireOp",EDGE,"E12"),sQuery(id+"F0.wireOp",EDGE,"E13.trimOffspring"),sQuery(id+"F0.wireOp",EDGE,"E14.filletArc"),sQuery(id+"F0.wireOp",EDGE,"E15.filletArc"),sQuery(id+"F0.wireOp",EDGE,"E16.filletArc"),sQuery(id+"F0.wireOp",EDGE,"E17.1.0"),sQuery(id+"F0.wireOp",EDGE,"E17.1.1"),sQuery(id+"F0.wireOp",EDGE,"E17.1.2"),sQuery(id+"F0.wireOp",EDGE,"E17.1.3"),sQuery(id+"F0.wireOp",EDGE,"E17.1.4"),sQuery(id+"F0.wireOp",EDGE,"E17.1.5"),sQuery(id+"F0.wireOp",EDGE,"E17.1.6"),sQuery(id+"F0.wireOp",EDGE,"E17.1.7"),sQuery(id+"F0.wireOp",EDGE,"E17.1.8"),sQuery(id+"F0.wireOp",EDGE,"E17.1.9"),sQuery(id+"F0.wireOp",EDGE,"E17.1.10"),sQuery(id+"F0.wireOp",EDGE,"E17.1.11"),sQuery(id+"F0.wireOp",EDGE,"E17.1.12"),sQuery(id+"F0.wireOp",EDGE,"E17.2.0"),sQuery(id+"F0.wireOp",EDGE,"E17.2.1"),sQuery(id+"F0.wireOp",EDGE,"E17.2.2"),sQuery(id+"F0.wireOp",EDGE,"E17.2.3"),sQuery(id+"F0.wireOp",EDGE,"E17.2.4"),sQuery(id+"F0.wireOp",EDGE,"E17.2.5"),sQuery(id+"F0.wireOp",EDGE,"E17.2.6"),sQuery(id+"F0.wireOp",EDGE,"E17.2.7"),sQuery(id+"F0.wireOp",EDGE,"E17.2.8"),sQuery(id+"F0.wireOp",EDGE,"E17.2.9"),sQuery(id+"F0.wireOp",EDGE,"E17.2.10"),sQuery(id+"F0.wireOp",EDGE,"E17.2.11"),sQuery(id+"F0.wireOp",EDGE,"E17.2.12"),sQuery(id+"F0.wireOp",EDGE,"E18.trimOffspring"),sQuery(id+"F0.wireOp",EDGE,"E19.trimOffspring")])],"isStart":true})});
            var Q7;
            Q7=makeQuery(id+"F9.boolean.opBoolean","SPLIT",FACE,{"disambiguationData":[TD([makeQuery(id+"F6.opExtrude","SWEPT_FACE",FACE,{"disambiguationData":[OSD([sQuery(id+"F2.wireOp",EDGE,"E20.sketch_text.stroke-55")])]})])],"derivedFrom":makeQuery(id+"F4.opExtrude","CAP_FACE",FACE,{"disambiguationData":[OSD([sQuery(id+"F0.wireOp",EDGE,"E0"),sQuery(id+"F0.wireOp",EDGE,"E2"),sQuery(id+"F0.wireOp",EDGE,"E3"),sQuery(id+"F0.wireOp",EDGE,"E4"),sQuery(id+"F0.wireOp",EDGE,"E5"),sQuery(id+"F0.wireOp",EDGE,"E6"),sQuery(id+"F0.wireOp",EDGE,"E7"),sQuery(id+"F0.wireOp",EDGE,"E8"),sQuery(id+"F0.wireOp",EDGE,"E9"),sQuery(id+"F0.wireOp",EDGE,"E10"),sQuery(id+"F0.wireOp",EDGE,"E12"),sQuery(id+"F0.wireOp",EDGE,"E13.trimOffspring"),sQuery(id+"F0.wireOp",EDGE,"E14.filletArc"),sQuery(id+"F0.wireOp",EDGE,"E15.filletArc"),sQuery(id+"F0.wireOp",EDGE,"E16.filletArc"),sQuery(id+"F0.wireOp",EDGE,"E17.1.0"),sQuery(id+"F0.wireOp",EDGE,"E17.1.1"),sQuery(id+"F0.wireOp",EDGE,"E17.1.2"),sQuery(id+"F0.wireOp",EDGE,"E17.1.3"),sQuery(id+"F0.wireOp",EDGE,"E17.1.4"),sQuery(id+"F0.wireOp",EDGE,"E17.1.5"),sQuery(id+"F0.wireOp",EDGE,"E17.1.6"),sQuery(id+"F0.wireOp",EDGE,"E17.1.7"),sQuery(id+"F0.wireOp",EDGE,"E17.1.8"),sQuery(id+"F0.wireOp",EDGE,"E17.1.9"),sQuery(id+"F0.wireOp",EDGE,"E17.1.10"),sQuery(id+"F0.wireOp",EDGE,"E17.1.11"),sQuery(id+"F0.wireOp",EDGE,"E17.1.12"),sQuery(id+"F0.wireOp",EDGE,"E17.2.0"),sQuery(id+"F0.wireOp",EDGE,"E17.2.1"),sQuery(id+"F0.wireOp",EDGE,"E17.2.2"),sQuery(id+"F0.wireOp",EDGE,"E17.2.3"),sQuery(id+"F0.wireOp",EDGE,"E17.2.4"),sQuery(id+"F0.wireOp",EDGE,"E17.2.5"),sQuery(id+"F0.wireOp",EDGE,"E17.2.6"),sQuery(id+"F0.wireOp",EDGE,"E17.2.7"),sQuery(id+"F0.wireOp",EDGE,"E17.2.8"),sQuery(id+"F0.wireOp",EDGE,"E17.2.9"),sQuery(id+"F0.wireOp",EDGE,"E17.2.10"),sQuery(id+"F0.wireOp",EDGE,"E17.2.11"),sQuery(id+"F0.wireOp",EDGE,"E17.2.12"),sQuery(id+"F0.wireOp",EDGE,"E18.trimOffspring"),sQuery(id+"F0.wireOp",EDGE,"E19.trimOffspring")])],"isStart":true})});
            var Q8;
            Q8=makeQuery(id+"F9.boolean.opBoolean","SPLIT",FACE,{"disambiguationData":[TD([makeQuery(id+"F9.opPattern","COPY",FACE,{"derivedFrom":makeQuery(id+"F6.opExtrude","SWEPT_FACE",FACE,{"disambiguationData":[OSD([sQuery(id+"F2.wireOp",EDGE,"E20.sketch_text.stroke-8")])]}),"instanceName":"2"})])],"derivedFrom":makeQuery(id+"F4.opExtrude","CAP_FACE",FACE,{"disambiguationData":[OSD([sQuery(id+"F0.wireOp",EDGE,"E0"),sQuery(id+"F0.wireOp",EDGE,"E2"),sQuery(id+"F0.wireOp",EDGE,"E3"),sQuery(id+"F0.wireOp",EDGE,"E4"),sQuery(id+"F0.wireOp",EDGE,"E5"),sQuery(id+"F0.wireOp",EDGE,"E6"),sQuery(id+"F0.wireOp",EDGE,"E7"),sQuery(id+"F0.wireOp",EDGE,"E8"),sQuery(id+"F0.wireOp",EDGE,"E9"),sQuery(id+"F0.wireOp",EDGE,"E10"),sQuery(id+"F0.wireOp",EDGE,"E12"),sQuery(id+"F0.wireOp",EDGE,"E13.trimOffspring"),sQuery(id+"F0.wireOp",EDGE,"E14.filletArc"),sQuery(id+"F0.wireOp",EDGE,"E15.filletArc"),sQuery(id+"F0.wireOp",EDGE,"E16.filletArc"),sQuery(id+"F0.wireOp",EDGE,"E17.1.0"),sQuery(id+"F0.wireOp",EDGE,"E17.1.1"),sQuery(id+"F0.wireOp",EDGE,"E17.1.2"),sQuery(id+"F0.wireOp",EDGE,"E17.1.3"),sQuery(id+"F0.wireOp",EDGE,"E17.1.4"),sQuery(id+"F0.wireOp",EDGE,"E17.1.5"),sQuery(id+"F0.wireOp",EDGE,"E17.1.6"),sQuery(id+"F0.wireOp",EDGE,"E17.1.7"),sQuery(id+"F0.wireOp",EDGE,"E17.1.8"),sQuery(id+"F0.wireOp",EDGE,"E17.1.9"),sQuery(id+"F0.wireOp",EDGE,"E17.1.10"),sQuery(id+"F0.wireOp",EDGE,"E17.1.11"),sQuery(id+"F0.wireOp",EDGE,"E17.1.12"),sQuery(id+"F0.wireOp",EDGE,"E17.2.0"),sQuery(id+"F0.wireOp",EDGE,"E17.2.1"),sQuery(id+"F0.wireOp",EDGE,"E17.2.2"),sQuery(id+"F0.wireOp",EDGE,"E17.2.3"),sQuery(id+"F0.wireOp",EDGE,"E17.2.4"),sQuery(id+"F0.wireOp",EDGE,"E17.2.5"),sQuery(id+"F0.wireOp",EDGE,"E17.2.6"),sQuery(id+"F0.wireOp",EDGE,"E17.2.7"),sQuery(id+"F0.wireOp",EDGE,"E17.2.8"),sQuery(id+"F0.wireOp",EDGE,"E17.2.9"),sQuery(id+"F0.wireOp",EDGE,"E17.2.10"),sQuery(id+"F0.wireOp",EDGE,"E17.2.11"),sQuery(id+"F0.wireOp",EDGE,"E17.2.12"),sQuery(id+"F0.wireOp",EDGE,"E18.trimOffspring"),sQuery(id+"F0.wireOp",EDGE,"E19.trimOffspring")])],"isStart":true})});
            var Q9;
            Q9=makeQuery(id+"F9.boolean.opBoolean","SPLIT",FACE,{"disambiguationData":[TD([makeQuery(id+"F9.opPattern","COPY",FACE,{"derivedFrom":makeQuery(id+"F6.opExtrude","SWEPT_FACE",FACE,{"disambiguationData":[OSD([sQuery(id+"F2.wireOp",EDGE,"E20.sketch_text.stroke-30")])]}),"instanceName":"2"})])],"derivedFrom":makeQuery(id+"F4.opExtrude","CAP_FACE",FACE,{"disambiguationData":[OSD([sQuery(id+"F0.wireOp",EDGE,"E0"),sQuery(id+"F0.wireOp",EDGE,"E2"),sQuery(id+"F0.wireOp",EDGE,"E3"),sQuery(id+"F0.wireOp",EDGE,"E4"),sQuery(id+"F0.wireOp",EDGE,"E5"),sQuery(id+"F0.wireOp",EDGE,"E6"),sQuery(id+"F0.wireOp",EDGE,"E7"),sQuery(id+"F0.wireOp",EDGE,"E8"),sQuery(id+"F0.wireOp",EDGE,"E9"),sQuery(id+"F0.wireOp",EDGE,"E10"),sQuery(id+"F0.wireOp",EDGE,"E12"),sQuery(id+"F0.wireOp",EDGE,"E13.trimOffspring"),sQuery(id+"F0.wireOp",EDGE,"E14.filletArc"),sQuery(id+"F0.wireOp",EDGE,"E15.filletArc"),sQuery(id+"F0.wireOp",EDGE,"E16.filletArc"),sQuery(id+"F0.wireOp",EDGE,"E17.1.0"),sQuery(id+"F0.wireOp",EDGE,"E17.1.1"),sQuery(id+"F0.wireOp",EDGE,"E17.1.2"),sQuery(id+"F0.wireOp",EDGE,"E17.1.3"),sQuery(id+"F0.wireOp",EDGE,"E17.1.4"),sQuery(id+"F0.wireOp",EDGE,"E17.1.5"),sQuery(id+"F0.wireOp",EDGE,"E17.1.6"),sQuery(id+"F0.wireOp",EDGE,"E17.1.7"),sQuery(id+"F0.wireOp",EDGE,"E17.1.8"),sQuery(id+"F0.wireOp",EDGE,"E17.1.9"),sQuery(id+"F0.wireOp",EDGE,"E17.1.10"),sQuery(id+"F0.wireOp",EDGE,"E17.1.11"),sQuery(id+"F0.wireOp",EDGE,"E17.1.12"),sQuery(id+"F0.wireOp",EDGE,"E17.2.0"),sQuery(id+"F0.wireOp",EDGE,"E17.2.1"),sQuery(id+"F0.wireOp",EDGE,"E17.2.2"),sQuery(id+"F0.wireOp",EDGE,"E17.2.3"),sQuery(id+"F0.wireOp",EDGE,"E17.2.4"),sQuery(id+"F0.wireOp",EDGE,"E17.2.5"),sQuery(id+"F0.wireOp",EDGE,"E17.2.6"),sQuery(id+"F0.wireOp",EDGE,"E17.2.7"),sQuery(id+"F0.wireOp",EDGE,"E17.2.8"),sQuery(id+"F0.wireOp",EDGE,"E17.2.9"),sQuery(id+"F0.wireOp",EDGE,"E17.2.10"),sQuery(id+"F0.wireOp",EDGE,"E17.2.11"),sQuery(id+"F0.wireOp",EDGE,"E17.2.12"),sQuery(id+"F0.wireOp",EDGE,"E18.trimOffspring"),sQuery(id+"F0.wireOp",EDGE,"E19.trimOffspring")])],"isStart":true})});
            var Q10;
            Q10=makeQuery(id+"F9.boolean.opBoolean","SPLIT",FACE,{"disambiguationData":[TD([makeQuery(id+"F9.opPattern","COPY",FACE,{"derivedFrom":makeQuery(id+"F6.opExtrude","SWEPT_FACE",FACE,{"disambiguationData":[OSD([sQuery(id+"F2.wireOp",EDGE,"E20.sketch_text.stroke-37")])]}),"instanceName":"2"})])],"derivedFrom":makeQuery(id+"F4.opExtrude","CAP_FACE",FACE,{"disambiguationData":[OSD([sQuery(id+"F0.wireOp",EDGE,"E0"),sQuery(id+"F0.wireOp",EDGE,"E2"),sQuery(id+"F0.wireOp",EDGE,"E3"),sQuery(id+"F0.wireOp",EDGE,"E4"),sQuery(id+"F0.wireOp",EDGE,"E5"),sQuery(id+"F0.wireOp",EDGE,"E6"),sQuery(id+"F0.wireOp",EDGE,"E7"),sQuery(id+"F0.wireOp",EDGE,"E8"),sQuery(id+"F0.wireOp",EDGE,"E9"),sQuery(id+"F0.wireOp",EDGE,"E10"),sQuery(id+"F0.wireOp",EDGE,"E12"),sQuery(id+"F0.wireOp",EDGE,"E13.trimOffspring"),sQuery(id+"F0.wireOp",EDGE,"E14.filletArc"),sQuery(id+"F0.wireOp",EDGE,"E15.filletArc"),sQuery(id+"F0.wireOp",EDGE,"E16.filletArc"),sQuery(id+"F0.wireOp",EDGE,"E17.1.0"),sQuery(id+"F0.wireOp",EDGE,"E17.1.1"),sQuery(id+"F0.wireOp",EDGE,"E17.1.2"),sQuery(id+"F0.wireOp",EDGE,"E17.1.3"),sQuery(id+"F0.wireOp",EDGE,"E17.1.4"),sQuery(id+"F0.wireOp",EDGE,"E17.1.5"),sQuery(id+"F0.wireOp",EDGE,"E17.1.6"),sQuery(id+"F0.wireOp",EDGE,"E17.1.7"),sQuery(id+"F0.wireOp",EDGE,"E17.1.8"),sQuery(id+"F0.wireOp",EDGE,"E17.1.9"),sQuery(id+"F0.wireOp",EDGE,"E17.1.10"),sQuery(id+"F0.wireOp",EDGE,"E17.1.11"),sQuery(id+"F0.wireOp",EDGE,"E17.1.12"),sQuery(id+"F0.wireOp",EDGE,"E17.2.0"),sQuery(id+"F0.wireOp",EDGE,"E17.2.1"),sQuery(id+"F0.wireOp",EDGE,"E17.2.2"),sQuery(id+"F0.wireOp",EDGE,"E17.2.3"),sQuery(id+"F0.wireOp",EDGE,"E17.2.4"),sQuery(id+"F0.wireOp",EDGE,"E17.2.5"),sQuery(id+"F0.wireOp",EDGE,"E17.2.6"),sQuery(id+"F0.wireOp",EDGE,"E17.2.7"),sQuery(id+"F0.wireOp",EDGE,"E17.2.8"),sQuery(id+"F0.wireOp",EDGE,"E17.2.9"),sQuery(id+"F0.wireOp",EDGE,"E17.2.10"),sQuery(id+"F0.wireOp",EDGE,"E17.2.11"),sQuery(id+"F0.wireOp",EDGE,"E17.2.12"),sQuery(id+"F0.wireOp",EDGE,"E18.trimOffspring"),sQuery(id+"F0.wireOp",EDGE,"E19.trimOffspring")])],"isStart":true})});
            var Q11;
            Q11=makeQuery(id+"F9.boolean.opBoolean","SPLIT",FACE,{"disambiguationData":[TD([makeQuery(id+"F9.opPattern","COPY",FACE,{"derivedFrom":makeQuery(id+"F6.opExtrude","SWEPT_FACE",FACE,{"disambiguationData":[OSD([sQuery(id+"F2.wireOp",EDGE,"E20.sketch_text.stroke-55")])]}),"instanceName":"2"})])],"derivedFrom":makeQuery(id+"F4.opExtrude","CAP_FACE",FACE,{"disambiguationData":[OSD([sQuery(id+"F0.wireOp",EDGE,"E0"),sQuery(id+"F0.wireOp",EDGE,"E2"),sQuery(id+"F0.wireOp",EDGE,"E3"),sQuery(id+"F0.wireOp",EDGE,"E4"),sQuery(id+"F0.wireOp",EDGE,"E5"),sQuery(id+"F0.wireOp",EDGE,"E6"),sQuery(id+"F0.wireOp",EDGE,"E7"),sQuery(id+"F0.wireOp",EDGE,"E8"),sQuery(id+"F0.wireOp",EDGE,"E9"),sQuery(id+"F0.wireOp",EDGE,"E10"),sQuery(id+"F0.wireOp",EDGE,"E12"),sQuery(id+"F0.wireOp",EDGE,"E13.trimOffspring"),sQuery(id+"F0.wireOp",EDGE,"E14.filletArc"),sQuery(id+"F0.wireOp",EDGE,"E15.filletArc"),sQuery(id+"F0.wireOp",EDGE,"E16.filletArc"),sQuery(id+"F0.wireOp",EDGE,"E17.1.0"),sQuery(id+"F0.wireOp",EDGE,"E17.1.1"),sQuery(id+"F0.wireOp",EDGE,"E17.1.2"),sQuery(id+"F0.wireOp",EDGE,"E17.1.3"),sQuery(id+"F0.wireOp",EDGE,"E17.1.4"),sQuery(id+"F0.wireOp",EDGE,"E17.1.5"),sQuery(id+"F0.wireOp",EDGE,"E17.1.6"),sQuery(id+"F0.wireOp",EDGE,"E17.1.7"),sQuery(id+"F0.wireOp",EDGE,"E17.1.8"),sQuery(id+"F0.wireOp",EDGE,"E17.1.9"),sQuery(id+"F0.wireOp",EDGE,"E17.1.10"),sQuery(id+"F0.wireOp",EDGE,"E17.1.11"),sQuery(id+"F0.wireOp",EDGE,"E17.1.12"),sQuery(id+"F0.wireOp",EDGE,"E17.2.0"),sQuery(id+"F0.wireOp",EDGE,"E17.2.1"),sQuery(id+"F0.wireOp",EDGE,"E17.2.2"),sQuery(id+"F0.wireOp",EDGE,"E17.2.3"),sQuery(id+"F0.wireOp",EDGE,"E17.2.4"),sQuery(id+"F0.wireOp",EDGE,"E17.2.5"),sQuery(id+"F0.wireOp",EDGE,"E17.2.6"),sQuery(id+"F0.wireOp",EDGE,"E17.2.7"),sQuery(id+"F0.wireOp",EDGE,"E17.2.8"),sQuery(id+"F0.wireOp",EDGE,"E17.2.9"),sQuery(id+"F0.wireOp",EDGE,"E17.2.10"),sQuery(id+"F0.wireOp",EDGE,"E17.2.11"),sQuery(id+"F0.wireOp",EDGE,"E17.2.12"),sQuery(id+"F0.wireOp",EDGE,"E18.trimOffspring"),sQuery(id+"F0.wireOp",EDGE,"E19.trimOffspring")])],"isStart":true})});
            extrude(context, id + "F11", {"entities" : qUnion([Q0, Q1, Q2, Q3, Q4, Q5, Q6, Q7, Q8, Q9, Q10, Q11]), "operationType" : NewBodyOperationType.REMOVE, "depth" : -2 * mm, "offsetDistance" : 25 * mm});
        }
        {
            var Q0;
            Q0=makeQuery(id+"F5.opExtrude","CAP_FACE",FACE,{"disambiguationData":[OSD([sQuery(id+"F3.wireOp",EDGE,"E21"),sQuery(id+"F3.wireOp",EDGE,"E22")])],"isStart":true});
            extrude(context, id + "F12", {"entities" : qUnion([Q0]), "operationType" : NewBodyOperationType.ADD, "surfaceOperationType" : NewSurfaceOperationType.ADD, "depth" : .5 * mm, "offsetDistance" : 25 * mm});
        }
    });
